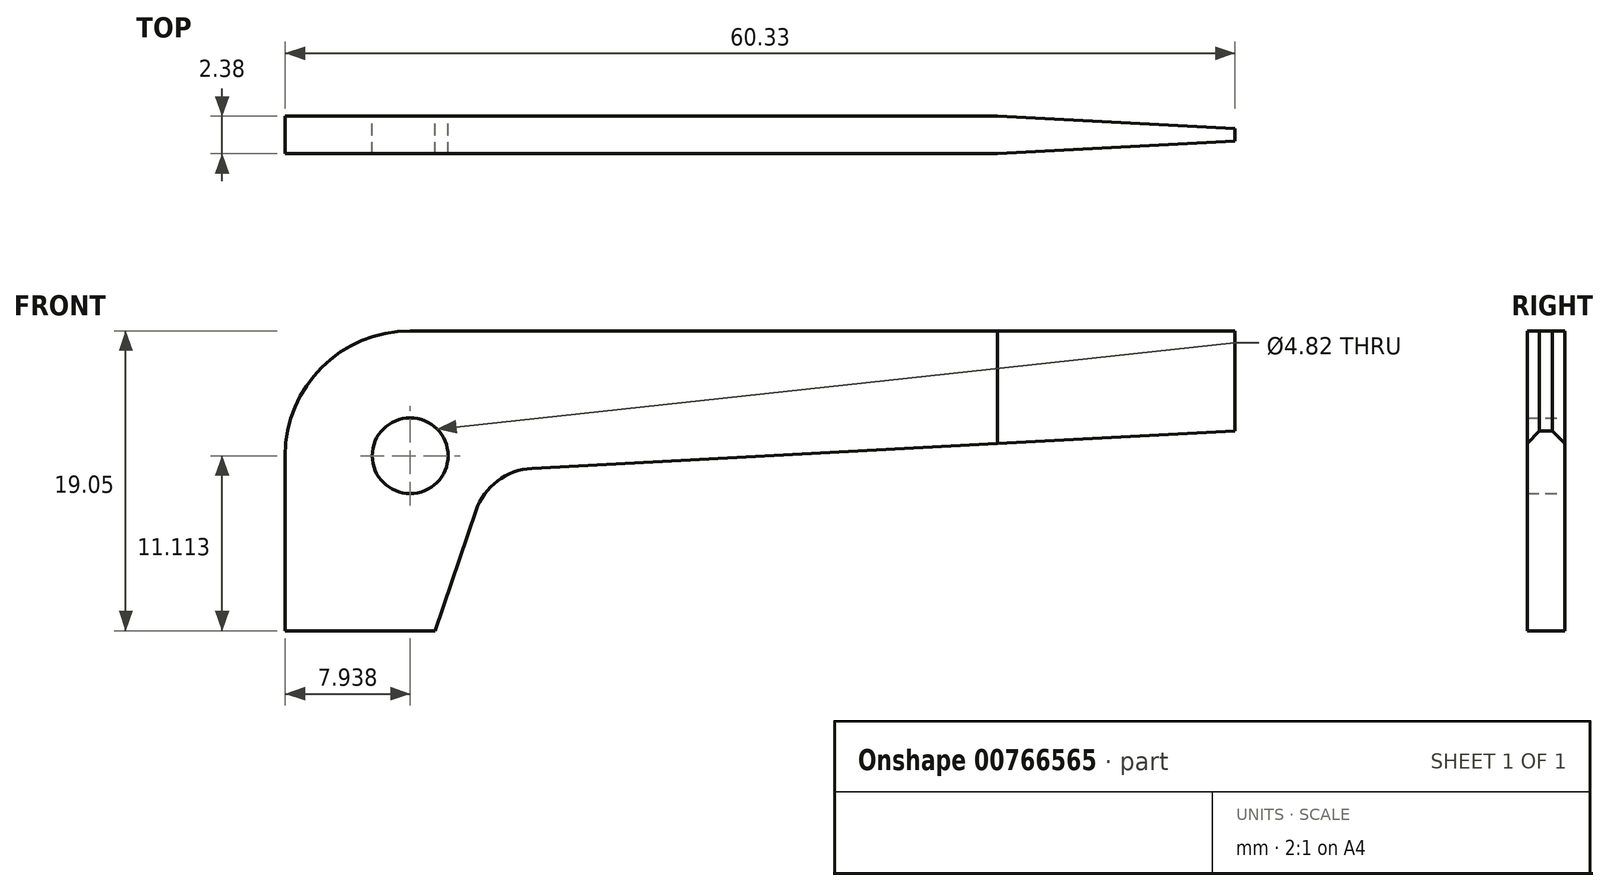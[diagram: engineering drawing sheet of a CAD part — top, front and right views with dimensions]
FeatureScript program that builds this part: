
annotation { "Feature Type Name" : "Feature", "Feature Type Description" : "" }
export const myFeature = defineFeature(function(context is Context, id is Id, definition is map)
    precondition{}
    {
        {
            var Q0;
            Q0=qCreatedBy(makeId("Front.planeOp"),FACE);
            var sketch = newSketch(context, id + "F0", { "sketchPlane" : qUnion([Q0])});
            skLineSegment(sketch, "E0.bottom", {"start": v(0, 0) * mm, "end": v(60.33, 0) * mm});
            skLineSegment(sketch, "E0.top", {"start": v(7.94, 19.05) * mm, "end": v(60.33, 19.05) * mm});
            skLineSegment(sketch, "E0.left", {"start": v(0, 0) * mm, "end": v(0, 11.11) * mm});
            skLineSegment(sketch, "E0.right", {"start": v(60.33, 0) * mm, "end": v(60.33, 19.05) * mm});
            skCircle(sketch, "E1", {"center": v(7.94, 11.11) * mm, "radius": 2.4 * mm});
            skPoint(sketch, "E2.visualSharp", {"position": v(0, 19.05) * mm});
            skArc(sketch, "E2.filletArc", {"start": v(7.94, 19.05) * mm, "mid": v(2.32, 16.73) * mm, "end": v(0, 11.11) * mm});
            skCircle(sketch, "E3", {"center": v(15.88, 6.35) * mm, "radius": 3.97 * mm});
            skLineSegment(sketch, "E4", {"start": v(0, 0) * mm, "end": v(9.53, 0) * mm});
            skLineSegment(sketch, "E5", {"start": v(9.53, 0) * mm, "end": v(12.12, 7.63) * mm});
            skLineSegment(sketch, "E6", {"start": v(60.33, 19.05) * mm, "end": v(60.33, 12.7) * mm});
            skLineSegment(sketch, "E7", {"start": v(60.33, 12.7) * mm, "end": v(15.66, 10.31) * mm});
            skSolve(sketch);
        }
        {
            var Q0;
            Q0=makeQuery(id+"F0.imprint","IMPRINT",FACE,{"disambiguationData":[TD([[makeQuery(id+"F0.imprint","IMPRINT",EDGE,{"derivedFrom":sQuery(id+"F0.wireOp",EDGE,"E0.top")}),-1.0]])]});
            extrude(context, id + "F1", {"entities" : qUnion([Q0]), "depth" : 2.38 * mm, "offsetDistance" : 25.4 * mm});
        }
        {
            var Q0;
            Q0=makeQuery(id+"F1.opExtrude","SWEPT_FACE",FACE,{"disambiguationData":[OSD([sQuery(id+"F0.wireOp",EDGE,"E0.top")])]});
            var sketch = newSketch(context, id + "F2", { "sketchPlane" : qUnion([Q0])});
            skLineSegment(sketch, "E8", {"start": v(60.33, 0) * mm, "end": v(60.33, -0.79) * mm});
            skLineSegment(sketch, "E9", {"start": v(60.33, -1.6) * mm, "end": v(45.24, -2.38) * mm});
            skLineSegment(sketch, "E10", {"start": v(60.33, -0.79) * mm, "end": v(45.24, 0) * mm});
            skLineSegment(sketch, "E11", {"start": v(60.33, 0) * mm, "end": v(45.24, 0) * mm});
            skLineSegment(sketch, "E12", {"start": v(45.24, -2.38) * mm, "end": v(60.33, -2.38) * mm});
            skLineSegment(sketch, "E13", {"start": v(60.33, -2.38) * mm, "end": v(60.33, -1.6) * mm});
            skSolve(sketch);
        }
        {
            var Q0;
            Q0 = qSketchRegion(id + "F2", true);
            extrude(context, id + "F3", {"entities" : qUnion([Q0]), "operationType" : NewBodyOperationType.REMOVE, "oppositeDirection" : true, "depth" : 25.4 * mm, "offsetDistance" : 25.4 * mm});
        }
    });
